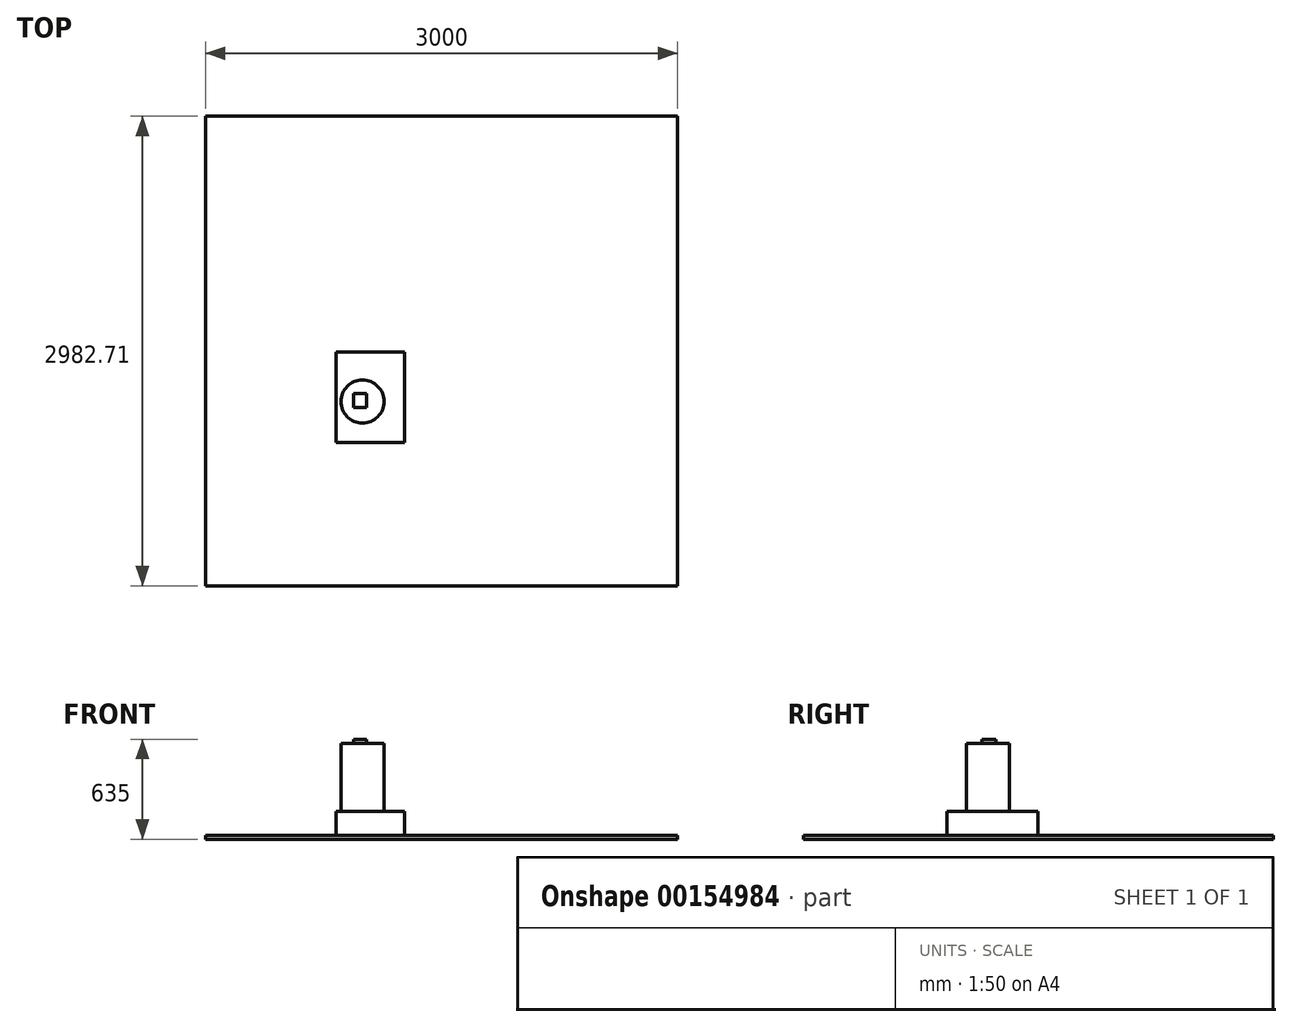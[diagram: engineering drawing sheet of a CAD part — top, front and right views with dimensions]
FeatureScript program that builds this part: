
annotation { "Feature Type Name" : "Feature", "Feature Type Description" : "" }
export const myFeature = defineFeature(function(context is Context, id is Id, definition is map)
    precondition{}
    {
        {
            var Q0;
            Q0=qCreatedBy(makeId("Top.planeOp"),FACE);
            var sketch = newSketch(context, id + "F0", { "sketchPlane" : qUnion([Q0])});
            skLineSegment(sketch, "E0.bottom", {"start": v(-1499, -1486.5) * mm, "end": v(1501, -1486.5) * mm});
            skLineSegment(sketch, "E0.top", {"start": v(-1499, 1496.2) * mm, "end": v(1501, 1496.2) * mm});
            skLineSegment(sketch, "E0.left", {"start": v(-1499, -1486.5) * mm, "end": v(-1499, 1496.2) * mm});
            skLineSegment(sketch, "E0.right", {"start": v(1501, -1486.5) * mm, "end": v(1501, 1496.2) * mm});
            skSolve(sketch);
        }
        {
            var Q0;
            Q0 = qSketchRegion(id + "F0", true);
            extrude(context, id + "F1", {"entities" : qUnion([Q0]), "depth" : 25.4 * mm});
        }
        {
            var Q0;
            Q0=makeQuery(id+"F1.opExtrude","CAP_FACE",FACE,{"disambiguationData":[OSD([sQuery(id+"F0.wireOp",EDGE,"E0.bottom"),sQuery(id+"F0.wireOp",EDGE,"E0.top"),sQuery(id+"F0.wireOp",EDGE,"E0.left"),sQuery(id+"F0.wireOp",EDGE,"E0.right")])],"isStart":false});
            var sketch = newSketch(context, id + "F2", { "sketchPlane" : qUnion([Q0])});
            skLineSegment(sketch, "E1.bottom", {"start": v(-670.05, -576.9) * mm, "end": v(-233.6, -576.9) * mm});
            skLineSegment(sketch, "E1.top", {"start": v(-670.05, 0) * mm, "end": v(-233.6, 0) * mm});
            skLineSegment(sketch, "E1.left", {"start": v(-670.05, -576.9) * mm, "end": v(-670.05, 0) * mm});
            skLineSegment(sketch, "E1.right", {"start": v(-233.6, -576.9) * mm, "end": v(-233.6, 0) * mm});
            skSolve(sketch);
        }
        {
            var Q0;
            Q0=makeQuery(id+"F2.imprint","IMPRINT",FACE,{"disambiguationData":[TD([[makeQuery(id+"F2.imprint","IMPRINT",EDGE,{"derivedFrom":sQuery(id+"F2.wireOp",EDGE,"E1.bottom")}),1.0]])]});
            extrude(context, id + "F3", {"entities" : qUnion([Q0]), "operationType" : NewBodyOperationType.ADD, "depth" : 152.4 * mm});
        }
        {
            var Q0;
            Q0=makeQuery(id+"F3.opExtrude","CAP_FACE",FACE,{"disambiguationData":[OSD([sQuery(id+"F2.wireOp",EDGE,"E1.bottom"),sQuery(id+"F2.wireOp",EDGE,"E1.top"),sQuery(id+"F2.wireOp",EDGE,"E1.left"),sQuery(id+"F2.wireOp",EDGE,"E1.right")])],"isStart":false});
            var sketch = newSketch(context, id + "F4", { "sketchPlane" : qUnion([Q0])});
            skCircle(sketch, "E2", {"center": v(-500.94, -316.06) * mm, "radius": 136.85 * mm});
            skSolve(sketch);
        }
        {
            var Q0;
            Q0 = qSketchRegion(id + "F4", true);
            extrude(context, id + "F5", {"entities" : qUnion([Q0]), "operationType" : NewBodyOperationType.ADD, "depth" : 431.8 * mm});
        }
        {
            var Q0;
            Q0=makeQuery(id+"F5.opExtrude","CAP_FACE",FACE,{"disambiguationData":[OSD([sQuery(id+"F4.wireOp",EDGE,"E2")])],"isStart":false});
            var sketch = newSketch(context, id + "F6", { "sketchPlane" : qUnion([Q0])});
            skLineSegment(sketch, "E3.bottom", {"start": v(-475.62, -353.32) * mm, "end": v(-558.35, -353.32) * mm});
            skLineSegment(sketch, "E3.top", {"start": v(-475.62, -264.9) * mm, "end": v(-558.35, -264.9) * mm});
            skLineSegment(sketch, "E3.left", {"start": v(-475.62, -353.32) * mm, "end": v(-475.62, -264.9) * mm});
            skLineSegment(sketch, "E3.right", {"start": v(-558.35, -353.32) * mm, "end": v(-558.35, -264.9) * mm});
            skSolve(sketch);
        }
        {
            var Q0;
            Q0 = qSketchRegion(id + "F6", true);
            extrude(context, id + "F7", {"entities" : qUnion([Q0]), "operationType" : NewBodyOperationType.ADD, "depth" : 25.4 * mm});
        }
    });
